# Revit family: Haworth_HiYa_MotorDriven_Rectangle_Desk_EU_PRELIMINARY
name_source: partatom
category: Furniture Systems
revit_build: Autodesk Revit 2018 (Build: 20170223_1515(x64)
units: mm (PartAtom-declared; Revit-internal decimal feet)

## family parameters
Always vertical = Yes
Cut with Voids When Loaded = No
OmniClass Number = 23.40.70.14.64.21
OmniClass Title = Systems Furniture
Part Type = Normal
Room Calculation Point = No
Round Connector Dimension = Use Diameter
Shared = No
Work Plane-Based = No

## types (4) — shared parameters
Actual Height = 65 cm
Assembly Code = E2020200
Box File = No
Cable Outlet Round = No
Cable Outlet U = No
Description = Haworth - HiYa - Motor Driven - Rectangular - Desk
Height = 65 cm
Hinged Doors = No
Leg Height = 62 cm
Manufacturer = Haworth, Inc.
Max. Depth = 90 cm
Max. Height = 130 cm
Max. Width = 180 cm
Min. Depth = 70 cm
Min. Height = 65 cm
Min. Width = 120 cm
Model = HYMLD
Open Drawer = No
Revision Number = 0
Size = Verify Final Dim. w/ Haworth
Standard Depths = 70, 80, 90 cm
Standard Widths = 120, 140, 160, 180 cm
Table Thickness = 3 cm
URL = https://www.haworth.com
URL - Product = https://www.haworth.com
Warranty = http://www.haworth.com

## per-type parameters (varying)
| type | Actual Depth | Actual Width | Cable Length | Cable Outlet Center | Connection Width | Open with Box Drawer | Screen Width | Sliding Door | Width |
| 160w x 80d - with Security Drawer | 80 cm | 160 cm | 120 cm | No | 138 cm | No | 162 cm | No | 160 cm |
| 140w x 90d - with Mobile Pedestal | 90 cm | 140 cm | 100 cm | Yes | 118 cm | No | 142 cm | Yes | 140 cm |
| 120w x 70d - with Suspended Pedestal | 70 cm | 120 cm | 80 cm | Yes | 98 cm | Yes | 122 cm | No | 120 cm |
| 180w x 90d - with Mobile Pedestal | 90 cm | 180 cm | 140 cm | No | 158 cm | No | 182 cm | Yes | 180 cm |

## geometry (parser evidence)
native form markers: Sweep x39
no freeform markers — native parametric forms only
